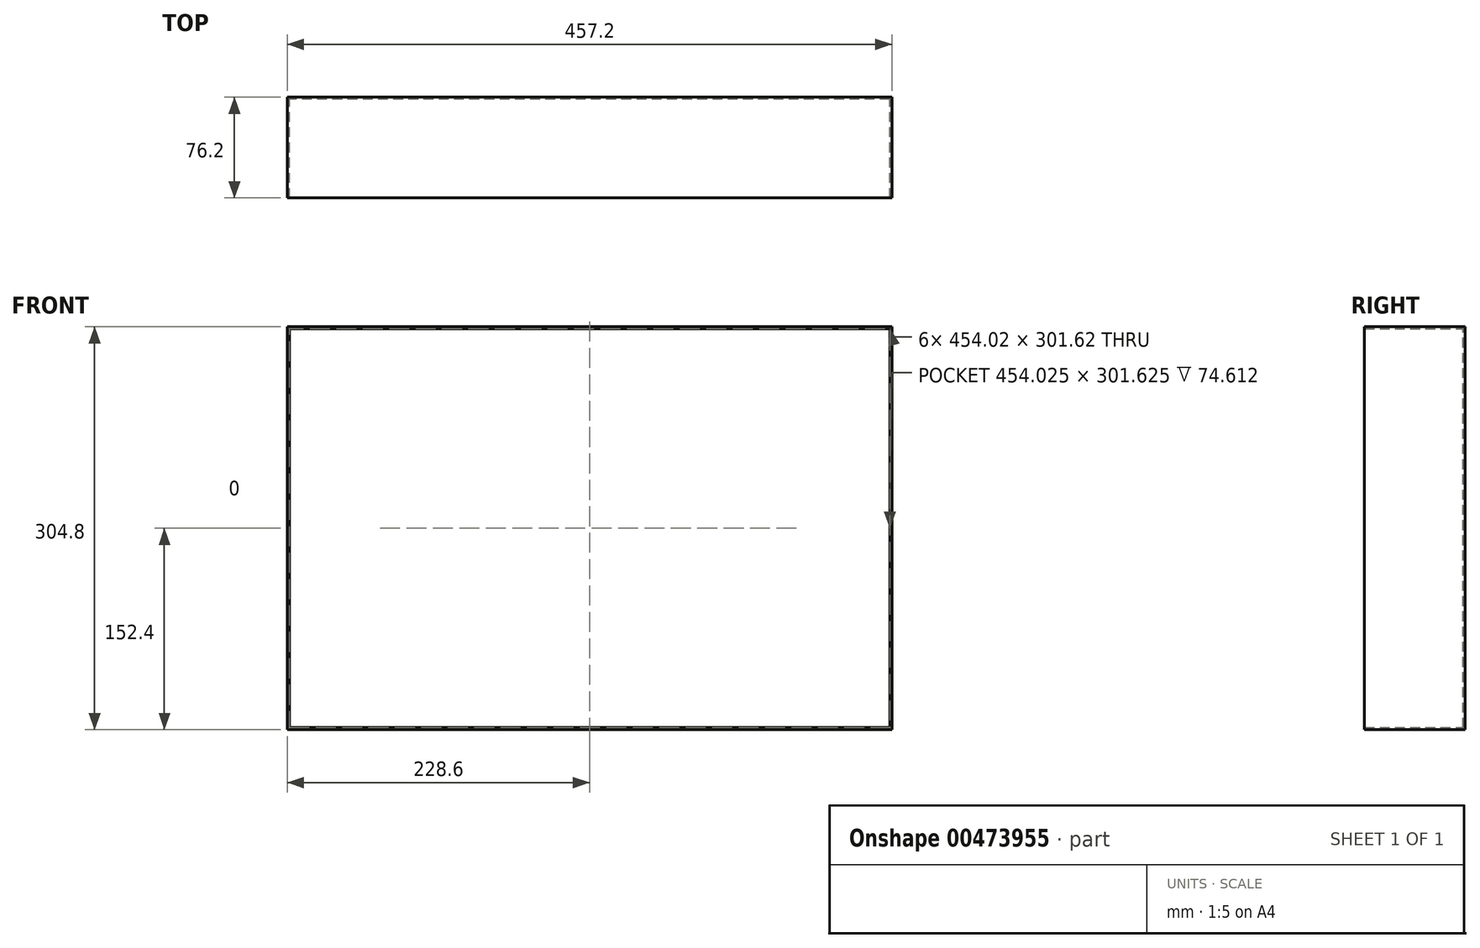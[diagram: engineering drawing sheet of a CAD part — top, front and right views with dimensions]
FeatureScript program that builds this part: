
annotation { "Feature Type Name" : "Feature", "Feature Type Description" : "" }
export const myFeature = defineFeature(function(context is Context, id is Id, definition is map)
    precondition{}
    {
        {
            var Q0;
            Q0=qCreatedBy(makeId("Front.planeOp"),FACE);
            var sketch = newSketch(context, id + "F0", { "sketchPlane" : qUnion([Q0])});
            skLineSegment(sketch, "E0.bottom", {"start": v(228.6, -152.4) * mm, "end": v(-228.6, -152.4) * mm});
            skLineSegment(sketch, "E0.top", {"start": v(228.6, 152.4) * mm, "end": v(-228.6, 152.4) * mm});
            skLineSegment(sketch, "E0.left", {"start": v(228.6, -152.4) * mm, "end": v(228.6, 152.4) * mm});
            skLineSegment(sketch, "E0.right", {"start": v(-228.6, -152.4) * mm, "end": v(-228.6, 152.4) * mm});
            skPoint(sketch, "E0.middle", {"position": v(0, 0) * mm});
            skSolve(sketch);
        }
        {
            var Q0;
            Q0 = qSketchRegion(id + "F0", true);
            extrude(context, id + "F1", {"entities" : qUnion([Q0]), "depth" : 76.2 * mm, "offsetDistance" : 25.4 * mm});
        }
        {
            var Q0;
            Q0=makeQuery(id+"F1.opExtrude","CAP_FACE",FACE,{"disambiguationData":[OSD([sQuery(id+"F0.wireOp",EDGE,"E0.bottom"),sQuery(id+"F0.wireOp",EDGE,"E0.top"),sQuery(id+"F0.wireOp",EDGE,"E0.left"),sQuery(id+"F0.wireOp",EDGE,"E0.right")])],"isStart":false});
            shell(context, id + "F2", {"entities" : qUnion([Q0]), "thickness" : 1.59 * mm});
        }
    });
